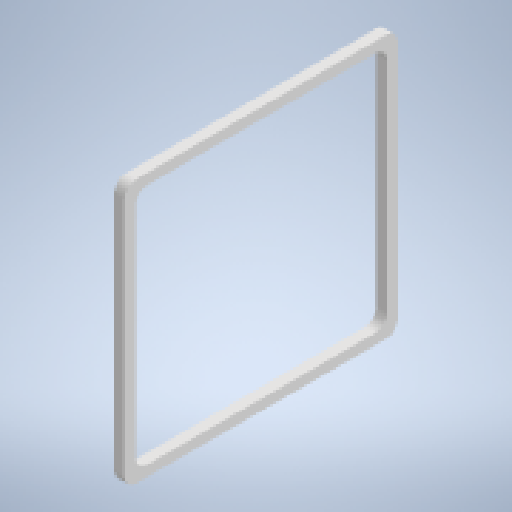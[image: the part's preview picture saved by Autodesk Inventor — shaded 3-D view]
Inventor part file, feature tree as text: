
AUTODESK INVENTOR PART (.ipt)
format: ipt  version: 2025.2 (Build 292293000, 293)  size: 163,328 bytes
history: native  units: mm
features: other x1, extrude x1, sketch x1
ambient origin geometry x8: Origin, YZ Plane, XZ Plane, XY Plane, X Axis, Y Axis, Z Axis, Center Point
bodies: Body1 (feature_tree)
feature tree (3):
  other  "Sólido1"
  extrude  "Extrusão1"  Depth=750.0mm
  sketch  "Esboço1"  dims[d0=780.0mm d1=750.0mm d2=30.0mm d3=35.0mm d4=35.0mm d5=35.0mm d6=30.0mm d7=0.0mm]
